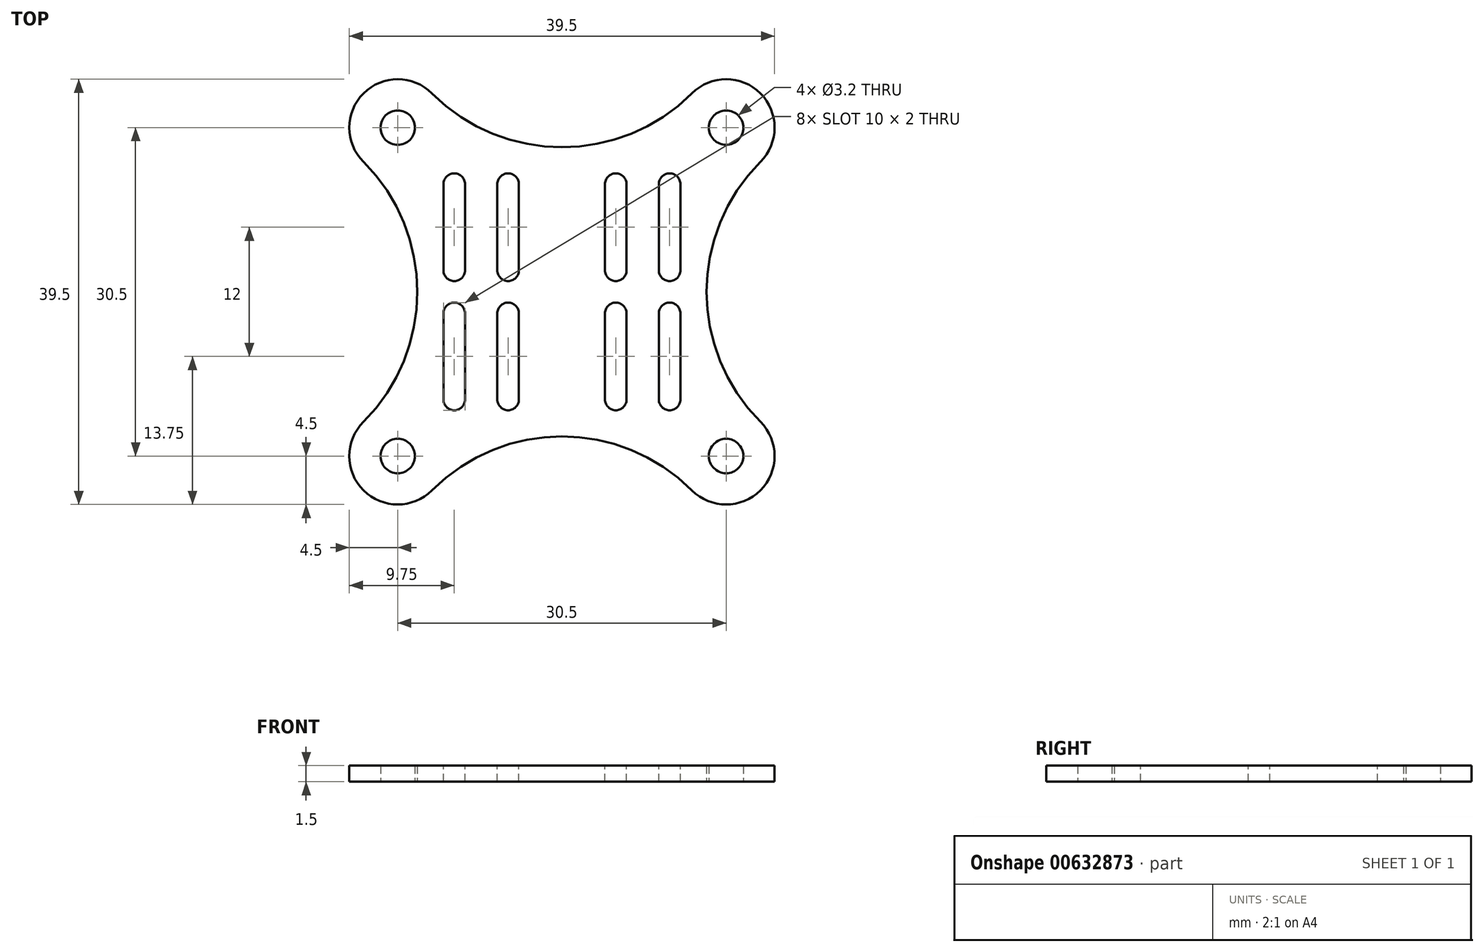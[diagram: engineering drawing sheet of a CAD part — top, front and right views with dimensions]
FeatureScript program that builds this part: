
annotation { "Feature Type Name" : "Feature", "Feature Type Description" : "" }
export const myFeature = defineFeature(function(context is Context, id is Id, definition is map)
    precondition{}
    {
        {
            var Q0;
            Q0=qCreatedBy(makeId("Top.planeOp"),FACE);
            var sketch = newSketch(context, id + "F0", { "sketchPlane" : qUnion([Q0])});
            skLineSegment(sketch, "E0.bottom", {"start": v(-15.25, 15.25) * mm, "end": v(15.25, 15.25) * mm, "construction": true});
            skLineSegment(sketch, "E0.top", {"start": v(-15.25, -15.25) * mm, "end": v(15.25, -15.25) * mm, "construction": true});
            skLineSegment(sketch, "E0.left", {"start": v(-15.25, 15.25) * mm, "end": v(-15.25, -15.25) * mm, "construction": true});
            skLineSegment(sketch, "E0.right", {"start": v(15.25, 15.25) * mm, "end": v(15.25, -15.25) * mm, "construction": true});
            skCircle(sketch, "E1", {"center": v(-15.25, 15.25) * mm, "radius": 1.6 * mm});
            skCircle(sketch, "E2", {"center": v(15.25, 15.25) * mm, "radius": 1.6 * mm});
            skCircle(sketch, "E3", {"center": v(15.25, -15.25) * mm, "radius": 1.6 * mm});
            skCircle(sketch, "E4", {"center": v(-15.25, -15.25) * mm, "radius": 1.6 * mm});
            skLineSegment(sketch, "E5", {"start": v(-30.5, 0) * mm, "end": v(0, 30.5) * mm, "construction": true});
            skLineSegment(sketch, "E6", {"start": v(0, 30.5) * mm, "end": v(30.5, 0) * mm, "construction": true});
            skLineSegment(sketch, "E7", {"start": v(30.5, 0) * mm, "end": v(0, -30.5) * mm, "construction": true});
            skLineSegment(sketch, "E8", {"start": v(0, -30.5) * mm, "end": v(-30.5, 0) * mm, "construction": true});
            skArc(sketch, "E9", {"start": v(-12.07, 18.43) * mm, "mid": v(-18.43, 18.43) * mm, "end": v(-18.43, 12.07) * mm});
            skArc(sketch, "E10", {"start": v(-12.07, -18.43) * mm, "mid": v(-18.43, -18.43) * mm, "end": v(-18.43, -12.07) * mm});
            skArc(sketch, "E11", {"start": v(18.43, 12.07) * mm, "mid": v(18.43, 18.43) * mm, "end": v(12.07, 18.43) * mm});
            skArc(sketch, "E12", {"start": v(18.43, -12.07) * mm, "mid": v(18.43, -18.43) * mm, "end": v(12.07, -18.43) * mm});
            skArc(sketch, "E13", {"start": v(12.07, -18.43) * mm, "mid": v(0, -13.43) * mm, "end": v(-12.07, -18.43) * mm});
            skArc(sketch, "E14", {"start": v(18.43, -12.07) * mm, "mid": v(13.43, 0) * mm, "end": v(18.43, 12.07) * mm});
            skArc(sketch, "E15", {"start": v(12.07, 18.43) * mm, "mid": v(0, 13.43) * mm, "end": v(-12.07, 18.43) * mm});
            skArc(sketch, "E16", {"start": v(-18.43, 12.07) * mm, "mid": v(-13.43, 0) * mm, "end": v(-18.43, -12.07) * mm});
            skSolve(sketch);
        }
        {
            var Q0;
            Q0 = qSketchRegion(id + "F0", true);
            extrude(context, id + "F1", {"entities" : qUnion([Q0]), "depth" : 1.5 * mm, "offsetDistance" : 25 * mm});
        }
        {
            var Q0;
            Q0=makeQuery(id+"F1.opExtrude","CAP_FACE",FACE,{"disambiguationData":[OSD([sQuery(id+"F0.wireOp",EDGE,"E1"),sQuery(id+"F0.wireOp",EDGE,"E2"),sQuery(id+"F0.wireOp",EDGE,"E3"),sQuery(id+"F0.wireOp",EDGE,"E4"),sQuery(id+"F0.wireOp",EDGE,"E9"),sQuery(id+"F0.wireOp",EDGE,"E10"),sQuery(id+"F0.wireOp",EDGE,"E11"),sQuery(id+"F0.wireOp",EDGE,"E12"),sQuery(id+"F0.wireOp",EDGE,"E13"),sQuery(id+"F0.wireOp",EDGE,"E14"),sQuery(id+"F0.wireOp",EDGE,"E15"),sQuery(id+"F0.wireOp",EDGE,"E16")])],"isStart":false});
            var sketch = newSketch(context, id + "F2", { "sketchPlane" : qUnion([Q0])});
            skLineSegment(sketch, "E17", {"start": v(-4, 10) * mm, "end": v(-4, 2) * mm});
            skLineSegment(sketch, "E18", {"start": v(-6, 10) * mm, "end": v(-6, 2) * mm});
            skArc(sketch, "E19", {"start": v(-4, 10) * mm, "mid": v(-5, 11) * mm, "end": v(-6, 10) * mm});
            skArc(sketch, "E20", {"start": v(-6, 2) * mm, "mid": v(-5, 1) * mm, "end": v(-4, 2) * mm});
            skLineSegment(sketch, "E21", {"start": v(4, 10) * mm, "end": v(4, 2) * mm});
            skLineSegment(sketch, "E22", {"start": v(6, 10) * mm, "end": v(6, 2) * mm});
            skArc(sketch, "E23", {"start": v(6, 10) * mm, "mid": v(5, 11) * mm, "end": v(4, 10) * mm});
            skArc(sketch, "E24", {"start": v(4, 2) * mm, "mid": v(5, 1) * mm, "end": v(6, 2) * mm});
            skLineSegment(sketch, "E25", {"start": v(-4, -2) * mm, "end": v(-4, -10) * mm});
            skLineSegment(sketch, "E26", {"start": v(-6, -2) * mm, "end": v(-6, -10) * mm});
            skArc(sketch, "E27", {"start": v(-4, -2) * mm, "mid": v(-5, -1) * mm, "end": v(-6, -2) * mm});
            skArc(sketch, "E28", {"start": v(-6, -10) * mm, "mid": v(-5, -11) * mm, "end": v(-4, -10) * mm});
            skLineSegment(sketch, "E29", {"start": v(4, -2) * mm, "end": v(4, -10) * mm});
            skLineSegment(sketch, "E30", {"start": v(6, -2) * mm, "end": v(6, -10) * mm});
            skArc(sketch, "E31", {"start": v(6, -2) * mm, "mid": v(5, -1) * mm, "end": v(4, -2) * mm});
            skArc(sketch, "E32", {"start": v(4, -10) * mm, "mid": v(5, -11) * mm, "end": v(6, -10) * mm});
            skLineSegment(sketch, "E33.left", {"start": v(-9, 10) * mm, "end": v(-9, 2) * mm});
            skLineSegment(sketch, "E33.right", {"start": v(-11, 10) * mm, "end": v(-11, 2) * mm});
            skArc(sketch, "E34", {"start": v(-9, 10) * mm, "mid": v(-10, 11) * mm, "end": v(-11, 10) * mm});
            skArc(sketch, "E35", {"start": v(-11, 2) * mm, "mid": v(-10, 1) * mm, "end": v(-9, 2) * mm});
            skLineSegment(sketch, "E36", {"start": v(-9, -2) * mm, "end": v(-9, -10) * mm});
            skLineSegment(sketch, "E37", {"start": v(-11, -2) * mm, "end": v(-11, -10) * mm});
            skArc(sketch, "E38", {"start": v(-9, -2) * mm, "mid": v(-10, -1) * mm, "end": v(-11, -2) * mm});
            skArc(sketch, "E39", {"start": v(-11, -10) * mm, "mid": v(-10, -11) * mm, "end": v(-9, -10) * mm});
            skLineSegment(sketch, "E40", {"start": v(9, -2) * mm, "end": v(9, -10) * mm});
            skLineSegment(sketch, "E41", {"start": v(11, -2) * mm, "end": v(11, -10) * mm});
            skArc(sketch, "E42", {"start": v(11, -2) * mm, "mid": v(10, -1) * mm, "end": v(9, -2) * mm});
            skArc(sketch, "E43", {"start": v(9, -10) * mm, "mid": v(10, -11) * mm, "end": v(11, -10) * mm});
            skLineSegment(sketch, "E44", {"start": v(9, 2) * mm, "end": v(9, 10) * mm});
            skLineSegment(sketch, "E45", {"start": v(11, 2) * mm, "end": v(11, 10) * mm});
            skArc(sketch, "E46", {"start": v(11, 10) * mm, "mid": v(10, 11) * mm, "end": v(9, 10) * mm});
            skArc(sketch, "E47", {"start": v(9, 2) * mm, "mid": v(10, 1) * mm, "end": v(11, 2) * mm});
            skSolve(sketch);
        }
        {
            var Q0;
            Q0 = qSketchRegion(id + "F2", true);
            extrude(context, id + "F3", {"entities" : qUnion([Q0]), "operationType" : NewBodyOperationType.REMOVE, "endBound" : BoundingType.THROUGH_ALL, "oppositeDirection" : true, "depth" : 25 * mm, "offsetDistance" : 25 * mm});
        }
    });
